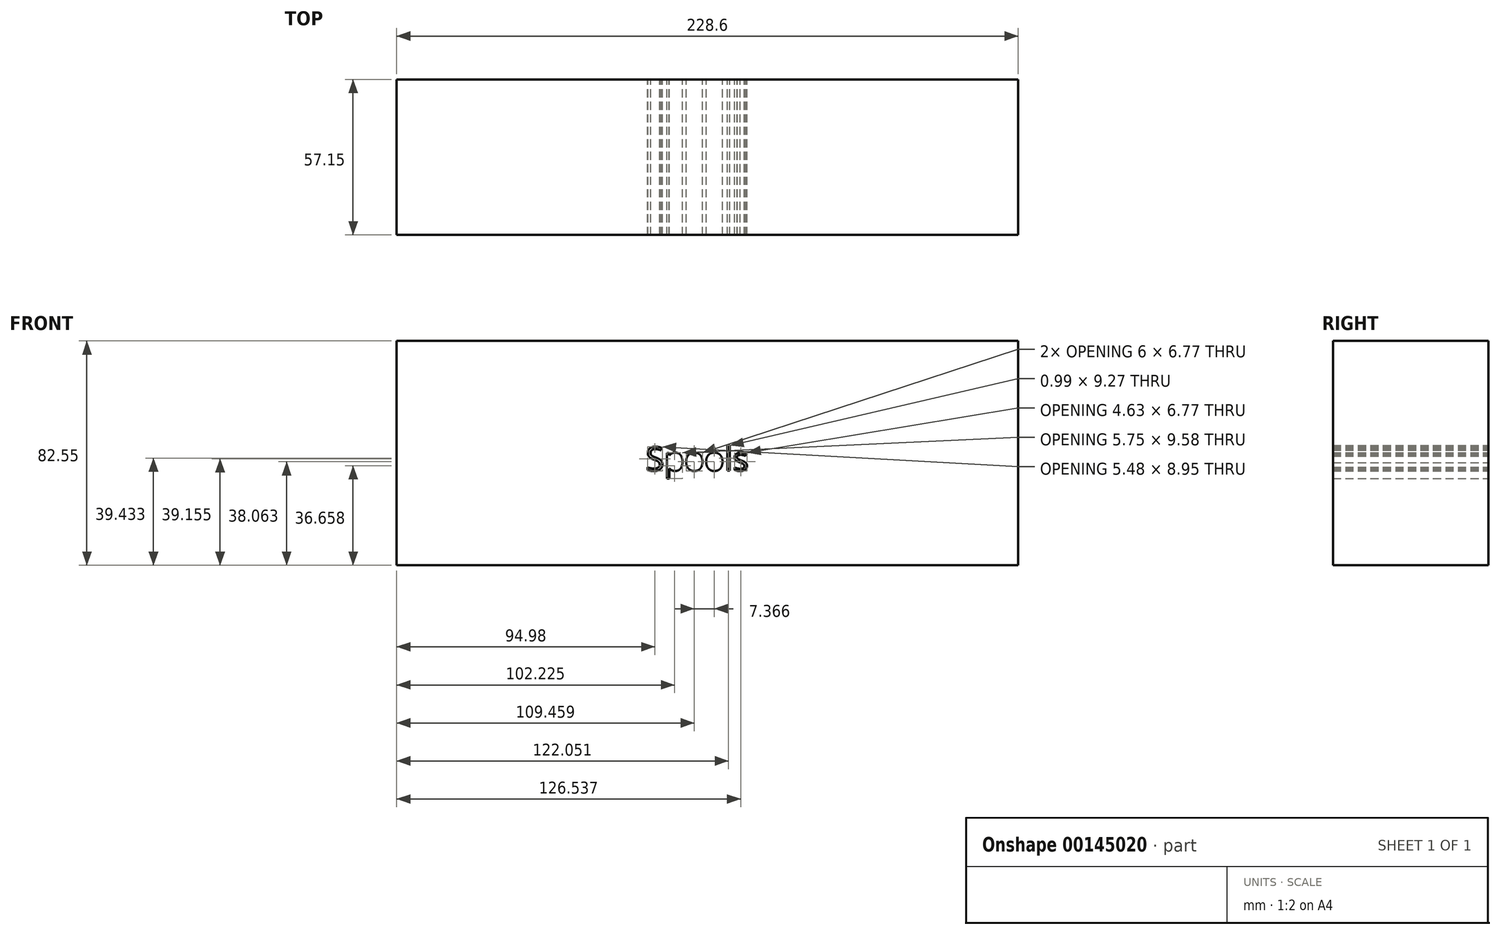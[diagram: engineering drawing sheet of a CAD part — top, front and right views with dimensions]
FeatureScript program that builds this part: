
annotation { "Feature Type Name" : "Feature", "Feature Type Description" : "" }
export const myFeature = defineFeature(function(context is Context, id is Id, definition is map)
    precondition{}
    {
        {
            var Q0;
            Q0=qCreatedBy(makeId("Front.planeOp"),FACE);
            var sketch = newSketch(context, id + "F0", { "sketchPlane" : qUnion([Q0])});
            skLineSegment(sketch, "E0.bottom", {"start": v(-110.7, 0) * mm, "end": v(117.9, 0) * mm});
            skLineSegment(sketch, "E0.top", {"start": v(-110.7, 82.55) * mm, "end": v(117.9, 82.55) * mm});
            skLineSegment(sketch, "E0.left", {"start": v(-110.7, 0) * mm, "end": v(-110.7, 82.55) * mm});
            skLineSegment(sketch, "E0.right", {"start": v(117.9, 0) * mm, "end": v(117.9, 82.55) * mm});
            skText(sketch, "E1", { "text": "Spools", "fontName": "OpenSans-Regular.ttf"});
            const initialGuessF0  = {"E1": [-0.0191, 0.0348, 1, 0, 0.00878]};
            skSetInitialGuess(sketch, initialGuessF0);
            skSolve(sketch);
        }
        {
            var Q0;
            Q0=makeQuery(id+"F0.imprint","IMPRINT",FACE,{"disambiguationData":[TD([[makeQuery(id+"F0.imprint","IMPRINT",EDGE,{"derivedFrom":sQuery(id+"F0.wireOp",EDGE,"E0.bottom")}),1.0]])]});
            extrude(context, id + "F1", {"entities" : qUnion([Q0]), "depth" : 57.15 * mm});
        }
    });
